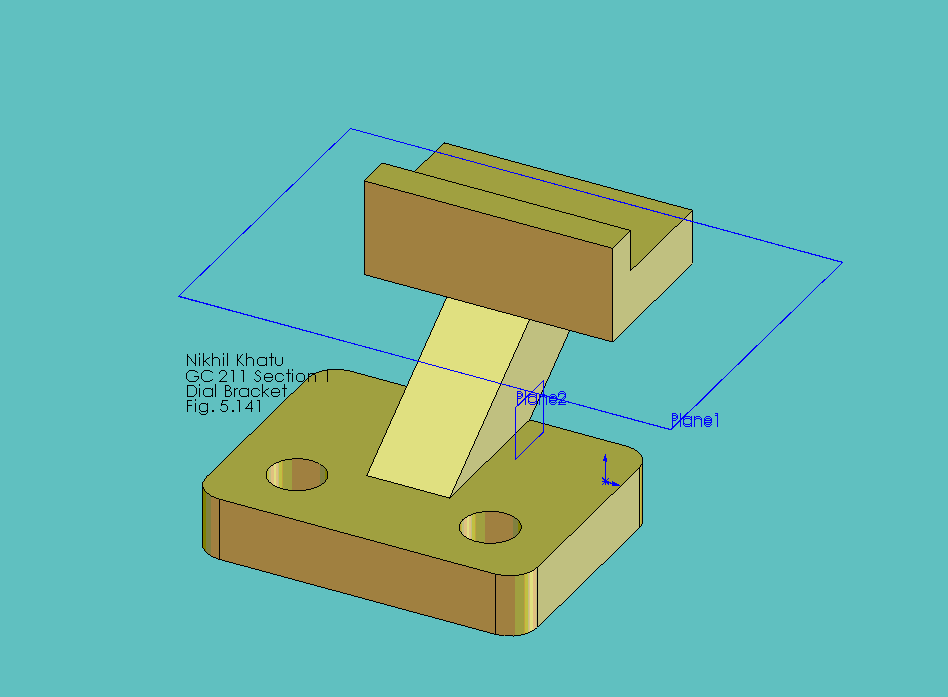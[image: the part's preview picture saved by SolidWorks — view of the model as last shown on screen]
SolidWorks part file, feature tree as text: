
SOLIDWORKS PART (.sldprt)
format: sldprt  version: not decoded by parser v0  size: 314,880 bytes
history: native  units: mm
features: plane x5, sketch x5, extrude x3, cut_extrude x2, material x1, fillet x1 (+11 scaffold rows collapsed)
feature tree (28):
  scaffold x11  (default folders/planes/origin — collapsed)
  material  "Pure Gold"
  plane  "Frontal"
  plane  "Horizontal"
  plane  "Profile"
  sketch  "Sketch1"  dims[D3=12.7mm D1=57.15mm D2=76.2mm D4=15.875mm D5=44.45mm D6=15.875mm D7=19.05mm D8=28.575mm]
  extrude  "Extrude2"  Depth=14.3002mm
  sketch  "Sketch2"  dims[D1=28.575mm D2=19.05mm D3=69.85mm D4=34.925mm]
  extrude  "Extrude3"  Depth=23.8252mm
  sketch  "Sketch3"
  cut_extrude  "Cut-Extrude1"  [1 undecoded]
  sketch  "Sketch4"
  cut_extrude  "Cut-Extrude2"  [1 undecoded]
  plane  "Plane1"  Offset=0mm
  plane  "Plane2"
  sketch  "Sketch5"  dims[D1=34.925mm D2=12.7mm D3=7.9502mm D4=22.225mm]
  extrude  "Extrude4"  Depth=19.05mm
  fillet  "Fillet1"  Radius=6.35mm
decode coverage: 7 of 11 modeling features carry decoded parameters
note: 2 parameter values undecoded
note: suppression state not decoded; provenance and decode notes live in map.json
